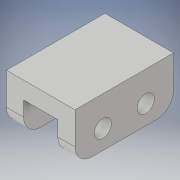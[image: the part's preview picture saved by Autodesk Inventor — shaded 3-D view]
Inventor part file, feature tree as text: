
AUTODESK INVENTOR PART (.ipt)
format: ipt  version: 2019 (Build 230136000, 136)  size: 153,088 bytes
history: native  units: mm
features: sketch x3, extrude x2, hole x1, fillet x1
ambient origin geometry x8: Origin, YZ Plane, XZ Plane, XY Plane, X Axis, Y Axis, Z Axis, Center Point
bodies: Solid1 (feature_tree)
feature tree (7):
  extrude  "Extrusion1"  Depth=80.0mm
  extrude  "Extrusion11"  Depth=20.0mm
  sketch  "Sketch13"  dims[d57=115.0mm d58=37.5mm d59=0.0mm d63=20.0mm d64=6.0mm d65=4.0mm d66=2.0mm d67=90.0deg d68=8.0mm d69=20.594885mm d120=20.0mm d129=25.0mm d130=25.0mm d131=15.0mm d12=1.0mm d13=1.0mm d14=1.0mm d15=0.15mm d16=0.25mm d17=0.375mm d18=14.3117mm d19=0.75mm d20=20.594885mm d21=0.0625mm d22=0.75mm d23=0.375mm]
  hole  "Hole2"  [1 undecoded]
  fillet  "Fillet19"  Radius=20.0mm
  sketch  "Sketch1"  dims[d0=115.0mm d1=80.0mm]
  sketch  "Sketch12"  dims[d2=20.0mm d3=0.0mm d56=20.0mm]
note: 1 required parameter value undecoded (feature->parameter linkage not recoverable at this tier; creation-order binding heuristic only, values carry confidence <= 0.55)
